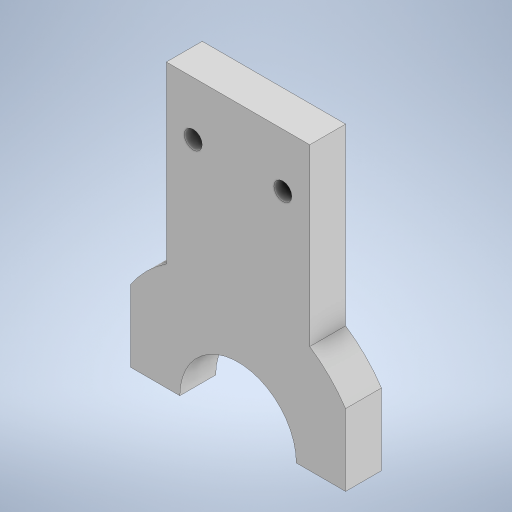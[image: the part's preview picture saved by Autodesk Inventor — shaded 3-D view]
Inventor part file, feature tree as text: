
AUTODESK INVENTOR PART (.ipt)
format: ipt  version: 2023 (Build 270158000, 158)  size: 239,104 bytes
history: native  units: in
note: dims shown in document units (in); Inventor stores cm internally (conversion verified against a paired STEP export)
features: extrude x1, sketch x1
ambient origin geometry x8: Origin, YZ Plane, XZ Plane, XY Plane, X Axis, Y Axis, Z Axis, Center Point
bodies: Body1 (feature_tree)
feature tree (2):
  extrude  "Extrusion3"  Depth=0.5in
  sketch  "Sketch1"  dims[d2=0.25in d3=0.25in d6=3.938in d7=1.625in d18=0.75in d19=0.75in d20=1.0in d21=1.0in d22=0.5in d23=0.0in d14=0.5in d15=0.0344in d16=0.5in d17=0.0344in]
